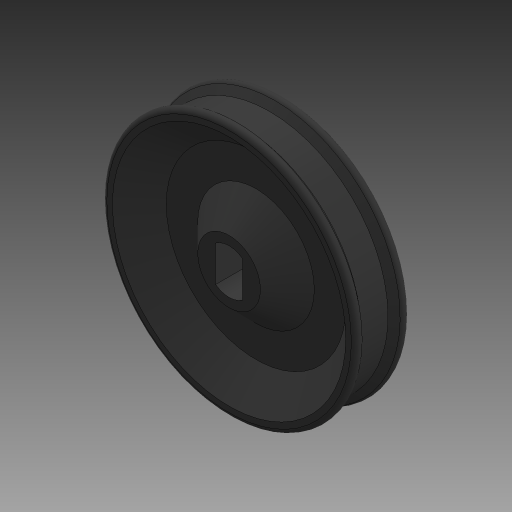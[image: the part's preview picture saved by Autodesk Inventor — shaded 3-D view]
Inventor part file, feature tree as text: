
AUTODESK INVENTOR PART (.ipt)
format: ipt  version: 2023 (Build 270158000, 158)  size: 355,328 bytes
history: native  units: mm
features: sketch x3, other x2, extrude x2, chamfer x2, fillet x1
ambient origin geometry x8: Origin, YZ Plane, XZ Plane, XY Plane, X Axis, Y Axis, Z Axis, Center Point
bodies: Body1 (feature_tree)
feature tree (10):
  other  "Těleso1"
  extrude  "Vysunutí1"  Depth=5.0mm
  other  "Rotace1"
  fillet  "Zaoblení1"  Radius=3.0mm
  extrude  "Vysunutí2"  Depth=5.0mm
  chamfer  "Zkosení1"  Distance=30.0mm
  chamfer  "Zkosení2"  Distance=6.0mm
  sketch  "Náčrt1"
  sketch  "Náčrt2"
  sketch  "Náčrt3"
